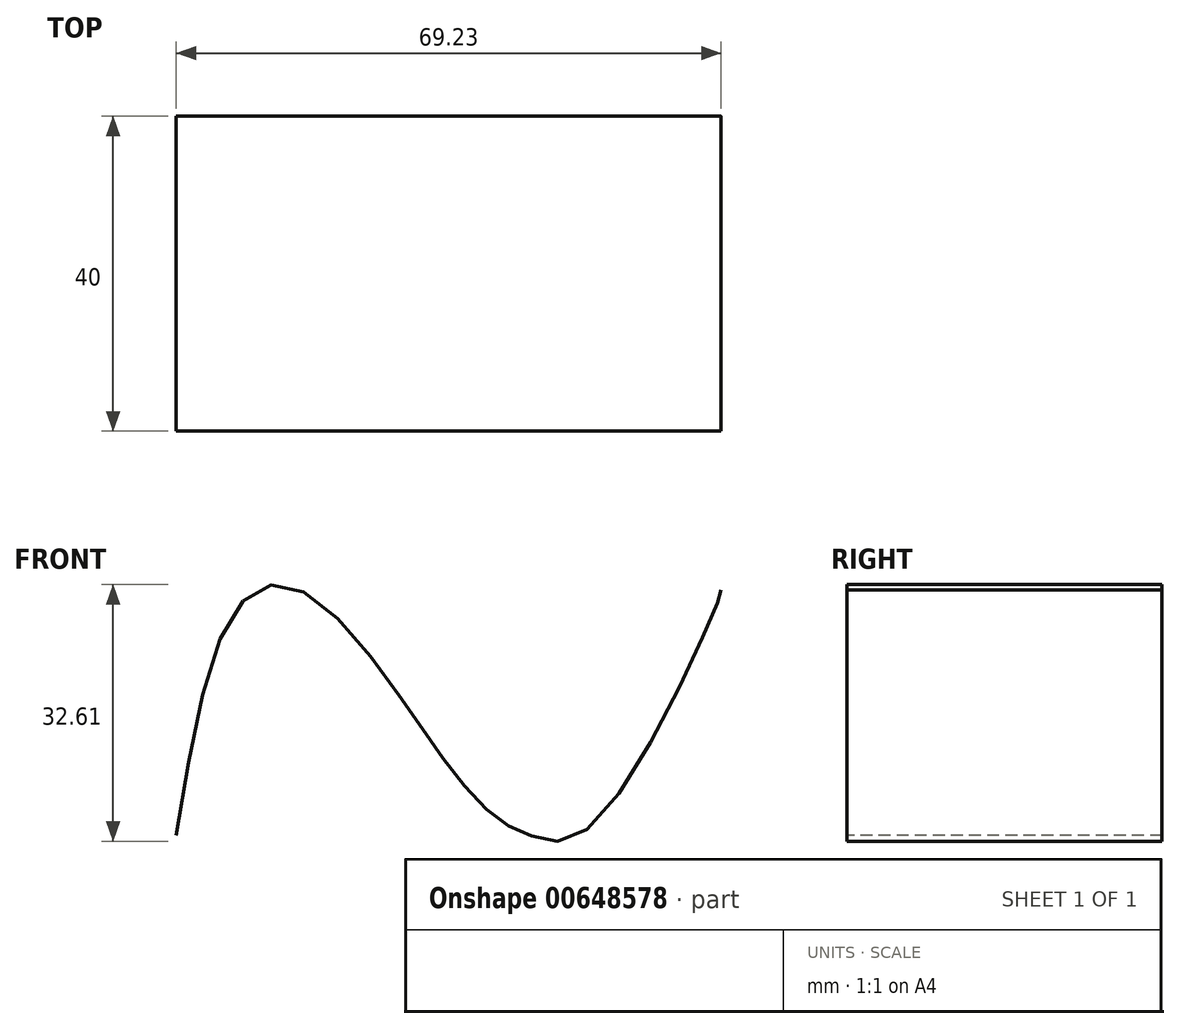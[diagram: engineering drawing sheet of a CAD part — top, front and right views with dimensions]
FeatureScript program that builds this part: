
annotation { "Feature Type Name" : "Feature", "Feature Type Description" : "" }
export const myFeature = defineFeature(function(context is Context, id is Id, definition is map)
    precondition{}
    {
        {
            var Q0;
            Q0=qCreatedBy(makeId("Front.planeOp"),FACE);
            var sketch = newSketch(context, id + "F0", { "sketchPlane" : qUnion([Q0])});
            skFitSpline(sketch, "E0", {"points": [v(0, 0) * mm, v(8.2, 29.5) * mm, v(15.69, 31.23) * mm, v(27.77, 18.56) * mm, v(34.68, 8.78) * mm, v(40.44, 2.45) * mm, v(45.04, 0) * mm, v(51.09, 0) * mm, v(64.61, 20.3) * mm, v(69.22, 30.94) * mm, v(69.22, 31.23) * mm], "startDerivative": vector(35.59, 217.13) * mm, "endDerivative": vector(-2.5, 12.39) * mm});
            skSolve(sketch);
        }
        {
            var Q0;
            Q0=sQuery(id+"F0.wireOp",EDGE,"E0");
            extrude(context, id + "F1", {"bodyType" : ToolBodyType.SURFACE, "surfaceEntities" : qUnion([Q0]), "depth" : 40 * mm, "offsetDistance" : 25.4 * mm});
        }
    });
